# Revit family: Indirect-Water-Heater_Lochinvar_Ltd-SIVS-66_G_E
name_source: partatom
category: Mechanical Equipment
revit_build: Autodesk Revit Architecture 2013 (Build: 20130531_2115(x64)
units: mm (PartAtom-declared; Revit-internal decimal feet)

## types (1)
- Indirect-Water-Heater_Lochinvar_Ltd-SIVS-66_G_E
    1e Maintenance (check-up) = 3 months after installation
    2nd Maintenance (general maintenance) = 12 months after installation
    Assembly Code = D3010
    BIM Content Developer = CAD & Company
    BIM Content Developer URL = http://www.cadcompany.nl
    Cold Water Connection R = 1"
    Description = Indirect Water Heater
    Destination / Counrty = UK & Ireland
    Diameter (with insulation) = 360 mm  [stored 1.1811 ft]
    Diameter (without insulation) = 303 mm  [stored 0.994094 ft]
    Draw-off Capacity @ ΔT = 28°C after 120 min. = 3347.0 L
    Draw-off Capacity @ ΔT = 28°C after 30 min. = 1228.0 L
    Draw-off Capacity @ ΔT = 28°C after 60 min. = 1934.0 L
    Draw-off Capacity @ ΔT = 28°C after 90 min. = 2641.0 L
    Draw-off Capacity @ ΔT = 44°C after 120 min. = 2130.0 L
    Draw-off Capacity @ ΔT = 44°C after 30 min. = 781.0 L
    Draw-off Capacity @ ΔT = 44°C after 60 min. = 1231.0 L
    Draw-off Capacity @ ΔT = 44°C after 90 min. = 1680.0 L
    Draw-off Capacity @ ΔT = 50°C after 120 min. = 1874.0 L
    Draw-off Capacity @ ΔT = 50°C after 30 min. = 688.0 L
    Draw-off Capacity @ ΔT = 50°C after 60 min. = 1083.0 L
    Draw-off Capacity @ ΔT = 50°C after 90 min. = 1479.0 L
    Draw-off Capacity @ ΔT = 55°C after 120 min. = 1704.0 L
    Draw-off Capacity @ ΔT = 55°C after 30 min. = 625.0 L
    Draw-off Capacity @ ΔT = 55°C after 60 min. = 985.0 L
    Draw-off Capacity @ ΔT = 55°C after 90 min. = 1344.0 L
    Draw-off Capacity @ ΔT = 70°C after 120 min. = 1339.0 L
    Draw-off Capacity @ ΔT = 70°C after 30 min. = 491.0 L
    Draw-off Capacity @ ΔT = 70°C after 60 min. = 774.0 L
    Draw-off Capacity @ ΔT = 70°C after 90 min. = 1056.0 L
    Empty Weight = 117.00 kg
    Flow Rate - Volume L/h = 1978
    Heating Up Time @ ΔT = 28°C = 13
    Heating Up Time @ ΔT = 44°C = 20
    Heating Up Time @ ΔT = 50°C = 22
    Heating Up Time @ ΔT = 55°C = 25
    Heating Up Time @ ΔT = 70°C = 31
    Height (with insulation) = 1370 mm  [stored 4.49475 ft]
    Height (without insulation) = 1313 mm  [stored 4.30774 ft]
    Height Cold Water Inlet = 75 mm
    Height Warm Water Outlet = 1310 mm  [stored 4.2979 ft]
    Hot / Warm Water Connection R = 1"
    Insulation Thickness = 57 mm  [stored 0.187008 ft]
    Length = 0 mm  [stored 0 ft]
    Maintenance Interval = 12 months
    Manufacturer = Lochinvar Limited
    Manufacturer Number = E 7110
E 7110
E 7110
    Max. Operating Pressure - heat exchanger = 1600000.0 Pa
    Max. Operating Pressure - tank = 1000000.0 Pa
    Max. Temperature - heat exchanger = 110 °C
    Max. Temperature - tank = 95 °C
    Model = SIVS 6 G E
    Nominal Output - heat exchanger = 46000 W
    Operating Weight = 417.00 kg
    Packaging Height = 1510 mm  [stored 4.95407 ft]
    Packaging Length = 780 mm  [stored 2.55906 ft]
    Packaging Width = 780 mm  [stored 2.55906 ft]
    Pressure Loss - heat exchanger 80ºC/60ºC = 5600.0 Pa
    Product Documentation Link = http://www.lochinvar.ltd.uk
    Product Instruction Link = http://www.lochinvar.ltd.uk
    Recovery Rate @ ΔT = 28°C (ltr/hr) = 1413
    Recovery Rate @ ΔT = 44°C (ltr/hr) = 899
    Recovery Rate @ ΔT = 50°C (ltr/hr) = 791
    Recovery Rate @ ΔT = 55°C (ltr/hr) = 719
    Recovery Rate @ ΔT = 70°C (ltr/hr) = 565
    Serial Number = 8717449269180
    Stand-by Loss = 0 W
    Stand-by Loss - daily (Watt/24H) = 0
    Storage Capacity - heat exchanger = 8.9 m³
    Storage Capacity - tank = 300 m³
    Surface Heat Exchanger = 1.47 m²
    T&P Connection Rp = 1"
    Transport Weight = 128.00 kg
    Type of Packaging = Plastic and Wood
    URL = www.lochinvar.ltd.uk
    Warranty on Parts = 12 months
    Warranty on Tank = 36 months
    Width = 0 mm  [stored 0 ft]
    Workspace = 820 mm  [stored 2.69029 ft]

note: [stored X ft] marks values corroborated as IEEE doubles in the binary element streams (Revit-internal decimal feet)

## geometry (parser evidence)
native form markers: Sweep x14
no freeform markers — native parametric forms only
